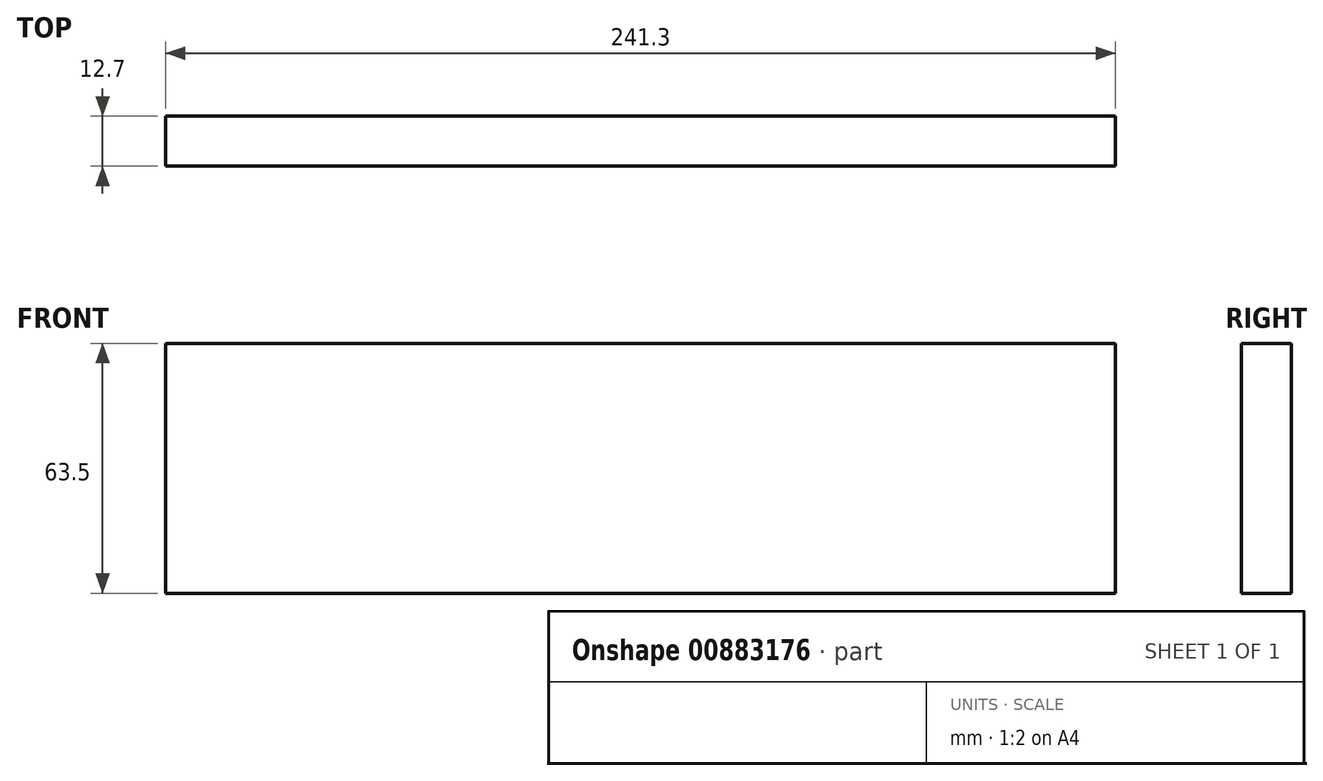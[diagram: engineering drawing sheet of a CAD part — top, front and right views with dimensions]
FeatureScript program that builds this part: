
annotation { "Feature Type Name" : "Feature", "Feature Type Description" : "" }
export const myFeature = defineFeature(function(context is Context, id is Id, definition is map)
    precondition{}
    {
        {
            var Q0;
            Q0=qCreatedBy(makeId("Front.planeOp"),FACE);
            var sketch = newSketch(context, id + "F0", { "sketchPlane" : qUnion([Q0])});
            skLineSegment(sketch, "E0.bottom", {"start": v(120.65, 31.75) * mm, "end": v(-120.65, 31.75) * mm});
            skLineSegment(sketch, "E0.top", {"start": v(120.65, -31.75) * mm, "end": v(-120.65, -31.75) * mm});
            skLineSegment(sketch, "E0.left", {"start": v(120.65, 31.75) * mm, "end": v(120.65, -31.75) * mm});
            skLineSegment(sketch, "E0.right", {"start": v(-120.65, 31.75) * mm, "end": v(-120.65, -31.75) * mm});
            skPoint(sketch, "E0.middle", {"position": v(0, 0) * mm});
            skSolve(sketch);
        }
        {
            var Q0;
            Q0=makeQuery(id+"F0.imprint","IMPRINT",FACE,{"disambiguationData":[TD([[makeQuery(id+"F0.imprint","IMPRINT",EDGE,{"derivedFrom":sQuery(id+"F0.wireOp",EDGE,"E0.bottom")}),1.0]])]});
            extrude(context, id + "F1", {"entities" : qUnion([Q0]), "oppositeDirection" : true, "depth" : 12.7 * mm, "offsetDistance" : 25.4 * mm});
        }
    });
